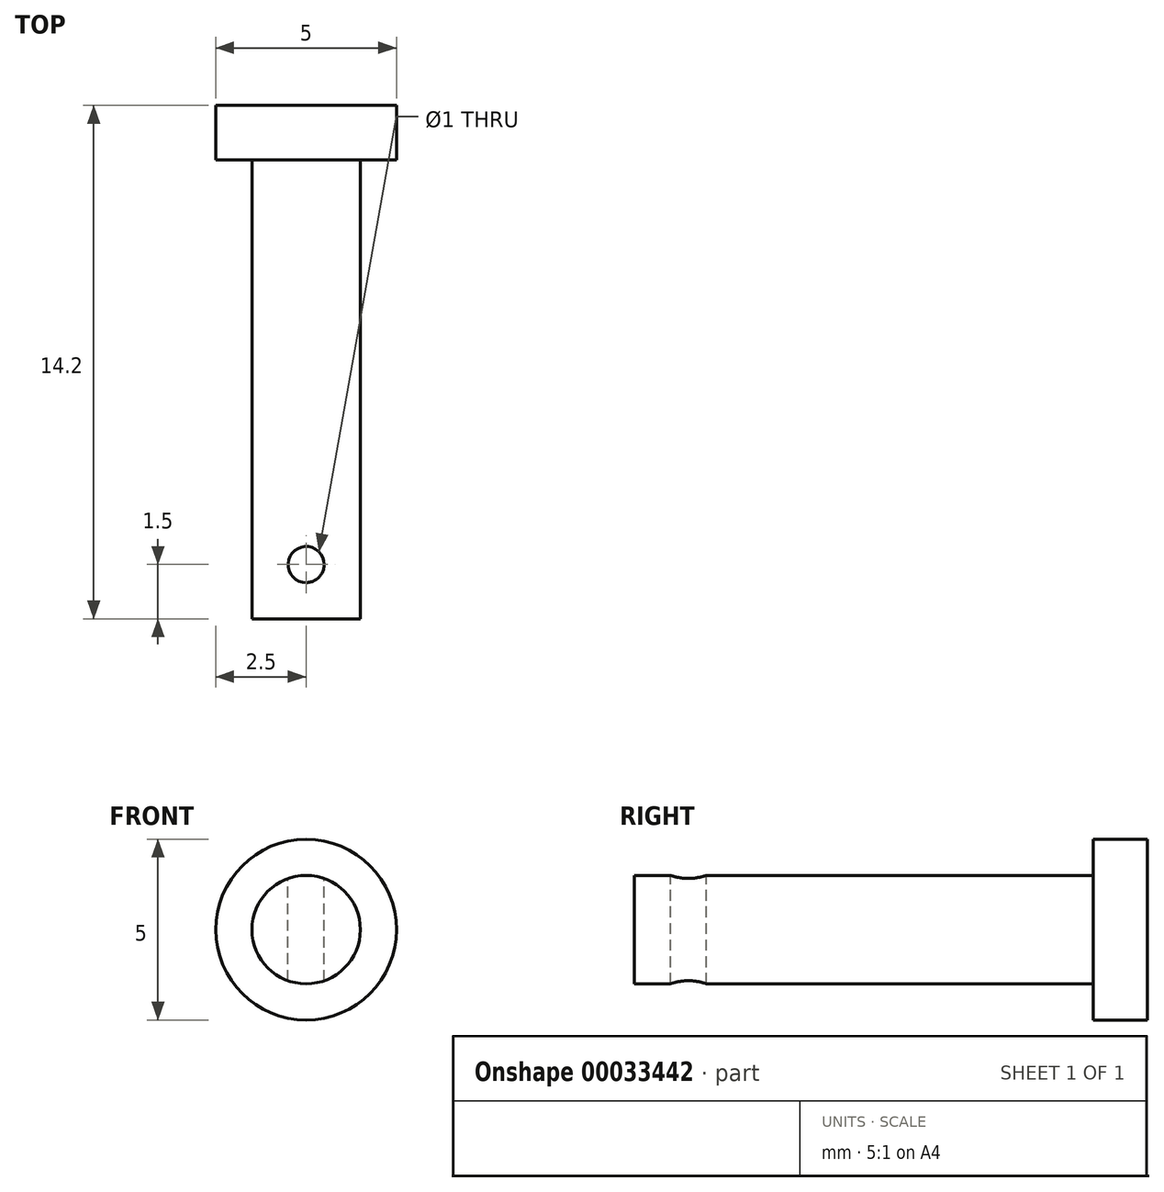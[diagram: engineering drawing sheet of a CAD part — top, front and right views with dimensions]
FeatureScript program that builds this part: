
annotation { "Feature Type Name" : "Feature", "Feature Type Description" : "" }
export const myFeature = defineFeature(function(context is Context, id is Id, definition is map)
    precondition{}
    {
        {
            var Q0;
            Q0=qCreatedBy(makeId("Front.planeOp"),FACE);
            var sketch = newSketch(context, id + "F0", { "sketchPlane" : qUnion([Q0])});
            skCircle(sketch, "E0", {"center": v(0, 0) * mm, "radius": 2.5 * mm});
            skSolve(sketch);
        }
        {
            var Q0;
            Q0=makeQuery(id+"F0.imprint","IMPRINT",FACE,{"disambiguationData":[TD([[makeQuery(id+"F0.imprint","IMPRINT",EDGE,{"derivedFrom":sQuery(id+"F0.wireOp",EDGE,"E0")}),1.0]])]});
            extrude(context, id + "F1", {"entities" : qUnion([Q0]), "depth" : 1.5 * mm});
        }
        {
            var Q0;
            Q0=makeQuery(id+"F1.opExtrude","CAP_FACE",FACE,{"disambiguationData":[OSD([sQuery(id+"F0.wireOp",EDGE,"E0")])],"isStart":false});
            var sketch = newSketch(context, id + "F2", { "sketchPlane" : qUnion([Q0])});
            skCircle(sketch, "E1", {"center": v(0, 0) * mm, "radius": 1.5 * mm});
            skSolve(sketch);
        }
        {
            var Q0;
            Q0=makeQuery(id+"F2.imprint","IMPRINT",FACE,{"disambiguationData":[TD([[makeQuery(id+"F2.imprint","IMPRINT",EDGE,{"derivedFrom":sQuery(id+"F2.wireOp",EDGE,"E1")}),1.0]])]});
            extrude(context, id + "F3", {"entities" : qUnion([Q0]), "operationType" : NewBodyOperationType.ADD, "depth" : 12.7 * mm});
        }
        {
            var Q0;
            Q0=qCreatedBy(makeId("Top.planeOp"),FACE);
            cPlane(context, id + "F4", {"entities" : qUnion([Q0]), "cplaneType" : CPlaneType.OFFSET, "offset" : 1.5 * mm, "width" : 150 * mm, "height" : 150 * mm});
        }
        {
            var Q0;
            Q0=qCreatedBy(id+"F4.planeOp",FACE);
            var sketch = newSketch(context, id + "F5", { "sketchPlane" : qUnion([Q0])});
            skCircle(sketch, "E2", {"center": v(0, -12.7) * mm, "radius": 0.5 * mm});
            skSolve(sketch);
        }
        {
            var Q0;
            Q0=makeQuery(id+"F5.imprint","IMPRINT",FACE,{"disambiguationData":[TD([[makeQuery(id+"F5.imprint","IMPRINT",EDGE,{"derivedFrom":sQuery(id+"F5.wireOp",EDGE,"E2")}),1.0]])]});
            var Q1;
            Q1=sQuery(id+"F5.wireOp",EDGE,"E2");
            extrude(context, id + "F6", {"entities" : qUnion([Q0]), "operationType" : NewBodyOperationType.REMOVE, "surfaceEntities" : qUnion([Q1]), "endBound" : BoundingType.THROUGH_ALL, "oppositeDirection" : true, "depth" : 25 * mm});
        }
    });
